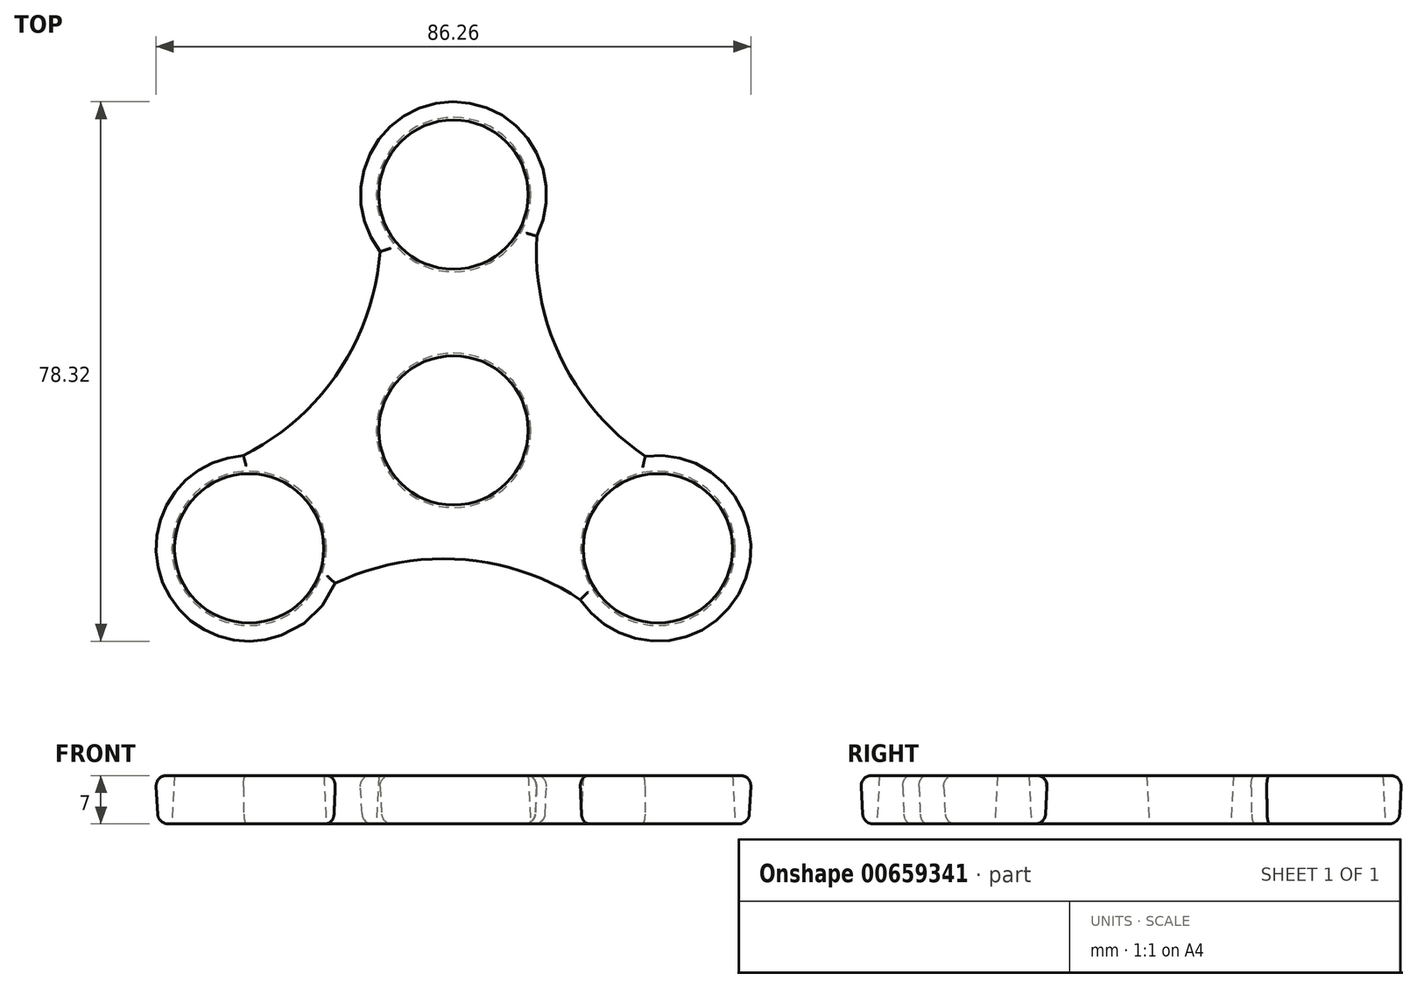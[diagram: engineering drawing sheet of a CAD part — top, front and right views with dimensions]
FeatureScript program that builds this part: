
annotation { "Feature Type Name" : "Feature", "Feature Type Description" : "" }
export const myFeature = defineFeature(function(context is Context, id is Id, definition is map)
    precondition{}
    {
        {
            var Q0;
            Q0=qCreatedBy(makeId("Top.planeOp"),FACE);
            var sketch = newSketch(context, id + "F0", { "sketchPlane" : qUnion([Q0])});
            skCircle(sketch, "E0", {"center": v(0, 0) * mm, "radius": 11.2 * mm});
            skCircle(sketch, "E1", {"center": v(0, 34.23) * mm, "radius": 11.2 * mm});
            skArc(sketch, "E2", {"start": v(11.8, 28.3) * mm, "mid": v(-1.33, 47.37) * mm, "end": v(-10.36, 26.05) * mm});
            skArc(sketch, "E3.1.0", {"start": v(-30.4, -3.94) * mm, "mid": v(-40.35, -24.84) * mm, "end": v(-17.38, -22) * mm});
            skCircle(sketch, "E3.1.1", {"center": v(-29.65, -17.12) * mm, "radius": 11.2 * mm});
            skArc(sketch, "E3.2.0", {"start": v(18.61, -24.36) * mm, "mid": v(41.69, -22.53) * mm, "end": v(27.74, -4.05) * mm});
            skCircle(sketch, "E3.2.1", {"center": v(29.65, -17.12) * mm, "radius": 11.2 * mm});
            skLineSegment(sketch, "E4", {"start": v(-19.91, -11.57) * mm, "end": v(-18.18, -10.58) * mm, "construction": true});
            skArc(sketch, "E5", {"start": v(11.8, 28.3) * mm, "mid": v(15.48, 10.01) * mm, "end": v(27.74, -4.05) * mm});
            skArc(sketch, "E6.1.0", {"start": v(-30.4, -3.94) * mm, "mid": v(-16.41, 8.4) * mm, "end": v(-10.36, 26.05) * mm});
            skArc(sketch, "E6.2.0", {"start": v(18.61, -24.36) * mm, "mid": v(0.93, -18.42) * mm, "end": v(-17.38, -22) * mm});
            skLineSegment(sketch, "E7.trimOffspring", {"start": v(9.83, 5.37) * mm, "end": v(11.56, 6.36) * mm, "construction": true});
            skLineSegment(sketch, "E8.trimOffspring", {"start": v(-11.37, -6.7) * mm, "end": v(-9.63, -5.71) * mm, "construction": true});
            skSolve(sketch);
        }
        {
            var Q0;
            Q0=makeQuery(id+"F0.imprint","IMPRINT",FACE,{"disambiguationData":[TD([[makeQuery(id+"F0.imprint","IMPRINT",EDGE,{"derivedFrom":sQuery(id+"F0.wireOp",EDGE,"E0")}),-1.0]])]});
            extrude(context, id + "F1", {"entities" : qUnion([Q0]), "depth" : 7 * mm, "offsetDistance" : 25 * mm, "hasDraft" : true, "draftAngle" : 3 * degree});
        }
        {
            var Q0;
            Q0=makeQuery(id+"F1.opExtrude","CAP_EDGE",EDGE,{"disambiguationData":[OSD([sQuery(id+"F0.wireOp",EDGE,"E6.2.0")])],"isStart":false});
            var Q1;
            Q1=makeQuery(id+"F1.opExtrude","CAP_EDGE",EDGE,{"disambiguationData":[OSD([sQuery(id+"F0.wireOp",EDGE,"E3.1.0")])],"isStart":false});
            var Q2;
            Q2=makeQuery(id+"F1.opExtrude","CAP_EDGE",EDGE,{"disambiguationData":[OSD([sQuery(id+"F0.wireOp",EDGE,"E6.1.0")])],"isStart":false});
            var Q3;
            Q3=makeQuery(id+"F1.opExtrude","CAP_EDGE",EDGE,{"disambiguationData":[OSD([sQuery(id+"F0.wireOp",EDGE,"E2")])],"isStart":false});
            var Q4;
            Q4=makeQuery(id+"F1.opExtrude","CAP_EDGE",EDGE,{"disambiguationData":[OSD([sQuery(id+"F0.wireOp",EDGE,"E5")])],"isStart":false});
            var Q5;
            Q5=makeQuery(id+"F1.opExtrude","CAP_EDGE",EDGE,{"disambiguationData":[OSD([sQuery(id+"F0.wireOp",EDGE,"E3.2.0")])],"isStart":false});
            fillet(context, id + "F2", {"entities" : qUnion([Q0, Q1, Q2, Q3, Q4, Q5]), "radius" : 1.5 * mm, "tangentPropagation" : true, "allowEdgeOverflow" : false});
        }
        {
            var Q0;
            Q0=makeQuery(id+"F1.opExtrude","CAP_EDGE",EDGE,{"disambiguationData":[OSD([sQuery(id+"F0.wireOp",EDGE,"E2")])],"isStart":true});
            var Q1;
            Q1=makeQuery(id+"F1.opExtrude","CAP_EDGE",EDGE,{"disambiguationData":[OSD([sQuery(id+"F0.wireOp",EDGE,"E6.1.0")])],"isStart":true});
            var Q2;
            Q2=makeQuery(id+"F1.opExtrude","CAP_EDGE",EDGE,{"disambiguationData":[OSD([sQuery(id+"F0.wireOp",EDGE,"E3.1.0")])],"isStart":true});
            var Q3;
            Q3=makeQuery(id+"F1.opExtrude","CAP_EDGE",EDGE,{"disambiguationData":[OSD([sQuery(id+"F0.wireOp",EDGE,"E6.2.0")])],"isStart":true});
            var Q4;
            Q4=makeQuery(id+"F1.opExtrude","CAP_EDGE",EDGE,{"disambiguationData":[OSD([sQuery(id+"F0.wireOp",EDGE,"E3.2.0")])],"isStart":true});
            var Q5;
            Q5=makeQuery(id+"F1.opExtrude","CAP_EDGE",EDGE,{"disambiguationData":[OSD([sQuery(id+"F0.wireOp",EDGE,"E5")])],"isStart":true});
            fillet(context, id + "F3", {"entities" : qUnion([Q0, Q1, Q2, Q3, Q4, Q5]), "radius" : 1.5 * mm, "tangentPropagation" : true, "allowEdgeOverflow" : false});
        }
    });
